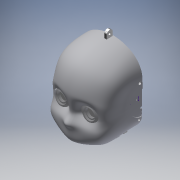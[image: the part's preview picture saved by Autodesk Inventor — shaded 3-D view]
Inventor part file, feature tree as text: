
AUTODESK INVENTOR PART (.ipt)
format: ipt  version: 2019 (Build 230136000, 136)  size: 8,108,544 bytes
history: native  units: in
note: dims shown in document units (in); Inventor stores cm internally (conversion verified against a paired STEP export)
features: sketch x30, extrude x23, other x18, plane x14, projected_geometry x7, mirror x6, surface_op x6, fillet x2, hole x2, thicken_offset x2, imported_body x2
ambient origin geometry x8: Origin, YZ Plane, XZ Plane, XY Plane, X Axis, Y Axis, Z Axis, Center Point
bodies: Solid6 (feature_tree), Solid2 (feature_tree)
feature tree (112):
  other  "rc_ist_009_p_077_09"
  other  "rc_ist_009_p_077_091"
  other  "Work Point1"
  other  "Work Point2"
  other  "Work Point3"
  other  "Work Point4"
  other  "Work Point5"
  other  "A_5"
  other  "A_6"
  other  "A_7"
  other  "A_8"
  other  "SIDE"
  other  "TOP"
  plane  "Work Plane4"
  plane  "Work Plane11"
  plane  "Work Plane7"
  plane  "Work Plane9"
  extrude  "Extrusion10"  Depth=0.9252in
  sketch  "Sketch11"  dims[d40=0.315in d41=0.315in]
  extrude  "Extrusion11"  Depth=0.315in
  plane  "Work Plane10"
  extrude  "Extrusion12"  Depth=1.063in TaperAngle=0.0deg
  mirror  "Mirror3"
  extrude  "Extrusion13"  Depth=1.8504in
  fillet  "Fillet1"  Radius=2.3622in
  fillet  "Fillet2"  Radius=0.3543in
  sketch  "Sketch15"  dims[d54=0.2756in d55=0.1969in d56=0.0in]
  extrude  "Extrusion14"  Depth=0.1969in TaperAngle=0.0deg
  extrude  "Extrusion15"  Depth=0.1969in TaperAngle=0.0deg
  extrude  "Extrusion16"  Depth=0.3937in
  extrude  "Extrusion17"  Depth=0.3937in
  extrude  "Extrusion18"  Depth=1.1811in
  extrude  "Extrusion19"  Depth=0.3937in
  hole  "Hole1"  [1 undecoded]
  hole  "Hole2"  [1 undecoded]
  extrude  "Extrusion22"  Depth=2.5591in
  extrude  "Extrusion23"  TaperAngle=150.0deg  [1 undecoded]
  extrude  "Extrusion24"  TaperAngle=60.0deg  [1 undecoded]
  extrude  "Extrusion25"  Depth=0.315in
  extrude  "Extrusion26"  Depth=0.3937in TaperAngle=0.0deg
  sketch  "Sketch34"  dims[d96=0.1969in d97=150.0deg]
  sketch  "3D Sketch2"
  surface_op  "Extend2"
  thicken_offset  "Thicken5"
  plane  "Work Plane12"
  extrude  "Extrusion27"  TaperAngle=150.0deg  [1 undecoded]
  plane  "Work Plane13"
  surface_op  "Extend3"
  thicken_offset  "Thicken6"
  mirror  "Mirror4"
  plane  "Work Plane14"
  plane  "Work Plane15"
  extrude  "Extrusion29"  TaperAngle=120.0deg  [1 undecoded]
  mirror  "Mirror5"
  plane  "Work Plane16"
  extrude  "Extrusion30"  TaperAngle=150.0deg  [1 undecoded]
  mirror  "Mirror6"
  extrude  "Extrusion31"  TaperAngle=120.0deg  [1 undecoded]
  plane  "Work Plane17"
  extrude  "Extrusion32"  Depth=0.7874in
  mirror  "Mirror8"
  extrude  "Extrusion33"  Depth=0.4331in
  extrude  "Extrusion34"  Depth=0.3937in
  mirror  "Mirror9"
  plane  "Work Plane19"
  plane  "Work Plane20"
  extrude  "Extrusion35"  Depth=0.3937in
  sketch  "3D Sketch1"
  other  "FRONT"
  imported_body  "Base1"
  imported_body  "Base2"
  plane  "Work Plane8"
  sketch  "Sketch10"  dims[d3=3.563in d35=0.9252in]
  sketch  "Sketch12"  dims[d42=0.315in d43=1.063in d44=0.0in]
  sketch  "Sketch13"  dims[d45=0.9252in d46=1.8504in d47=2.3622in d48=0.0in d49=0.3543in]
  sketch  "Sketch14"  dims[d50=0.3543in d52=0.1969in d53=0.0in]
  projected_geometry  "Projected Loop6"
  sketch  "Sketch16"  dims[d57=0.3937in d58=0.3937in]
  sketch  "Sketch17"  dims[d59=0.2362in d60=0.0in d61=0.3937in]
  projected_geometry  "Projected Loop7"
  projected_geometry  "Projected Loop8"
  projected_geometry  "Projected Loop9"
  sketch  "Sketch18"  dims[d62=180.0deg d63=1.1811in]
  projected_geometry  "Projected Loop10"
  sketch  "Sketch19"  dims[d64=90.0deg d65=0.3937in]
  projected_geometry  "Projected Loop11"
  sketch  "Sketch21"  dims[d66=90.0deg d67=3.937in d68=0.0in]
  sketch  "Sketch22"  dims[d73=0.3937in d75=3.937in d76=0.0in]
  sketch  "Sketch26"  dims[d77=3.937in d78=0.0in d82=2.5591in]
  sketch  "Sketch27"  dims[d83=2.5591in d84=150.0deg]
  sketch  "Sketch29"  dims[d85=0.315in d86=60.0deg]
  sketch  "Sketch30"  dims[d87=30.0deg d88=0.315in]
  sketch  "Sketch31"  dims[d89=60.0deg d90=0.3937in d91=0.0in]
  sketch  "Sketch32"  dims[d92=0.1969in d93=150.0deg]
  sketch  "Sketch33"  dims[d94=0.1969in d95=120.0deg]
  other  "Srf6"
  sketch  "Sketch35"  dims[d98=0.1969in d99=120.0deg]
  other  "Srf7"
  other  "Srf11"
  other  "Srf10"
  sketch  "Sketch38"  dims[d100=0.3937in d101=0.0in d108=0.7874in]
  sketch  "Sketch39"  dims[d109=0.2953in]
  sketch  "Sketch41"  dims[d110=0.2953in d111=0.2362in d112=0.1575in d113=0.0787in d114=90.0deg d115=0.315in d116=0.8108in d117=0.4331in]
  sketch  "Sketch42"  dims[d118=0.4724in d119=0.2362in d120=0.1575in d121=0.0787in d122=90.0deg d123=0.1969in d124=0.0in d127=0.3937in]
  sketch  "Sketch43"  dims[d128=0.1969in d129=0.0in d130=0.3937in]
  sketch  "Sketch44"  dims[d131=0.1969in d132=0.0in]
  projected_geometry  "Projected Loop12"
  sketch  "Sketch49"  dims[d133=0.7087in d134=0.1575in d135=0.0in d136=0.5906in d137=0.1575in d138=0.0in d139=0.3937in d140=0.0in d153=0.1969in d154=0.0in d158=0.1181in d160=0.3937in d161=-0.815in d162=0.0in d163=0.0in d165=0.8465in d166=1.0625in d169=0.1969in d170=0.0in d171=0.1575in d172=0.1575in d173=0.1575in d185=0.3937in d190=0.0in d191=-1.6063in d192=0.315in d193=0.3937in d194=0.0787in d195=0.3937in d196=0.0in d197=1.7913in d200=0.315in d201=0.3937in d202=0.0in d203=0.0787in d204=0.3937in d205=0.0in d213=0.1378in d214=0.1969in d215=0.1181in d216=0.3937in d217=0.0in d218=0.2362in d219=0.1181in d220=0.0in d221=0.1378in d222=0.1969in d223=0.1378in d224=0.0787in d225=0.0in d226=0.2362in d227=0.1181in d228=0.0in d229=0.3937in d230=0.0in]
  surface_op  "Boundary Patch2"
  surface_op  "Boundary Patch3"
  surface_op  "Boundary Patch6"
  surface_op  "Boundary Patch7"
note: 8 required parameter values undecoded (feature->parameter linkage not recoverable at this tier; creation-order binding heuristic only, values carry confidence <= 0.55)
